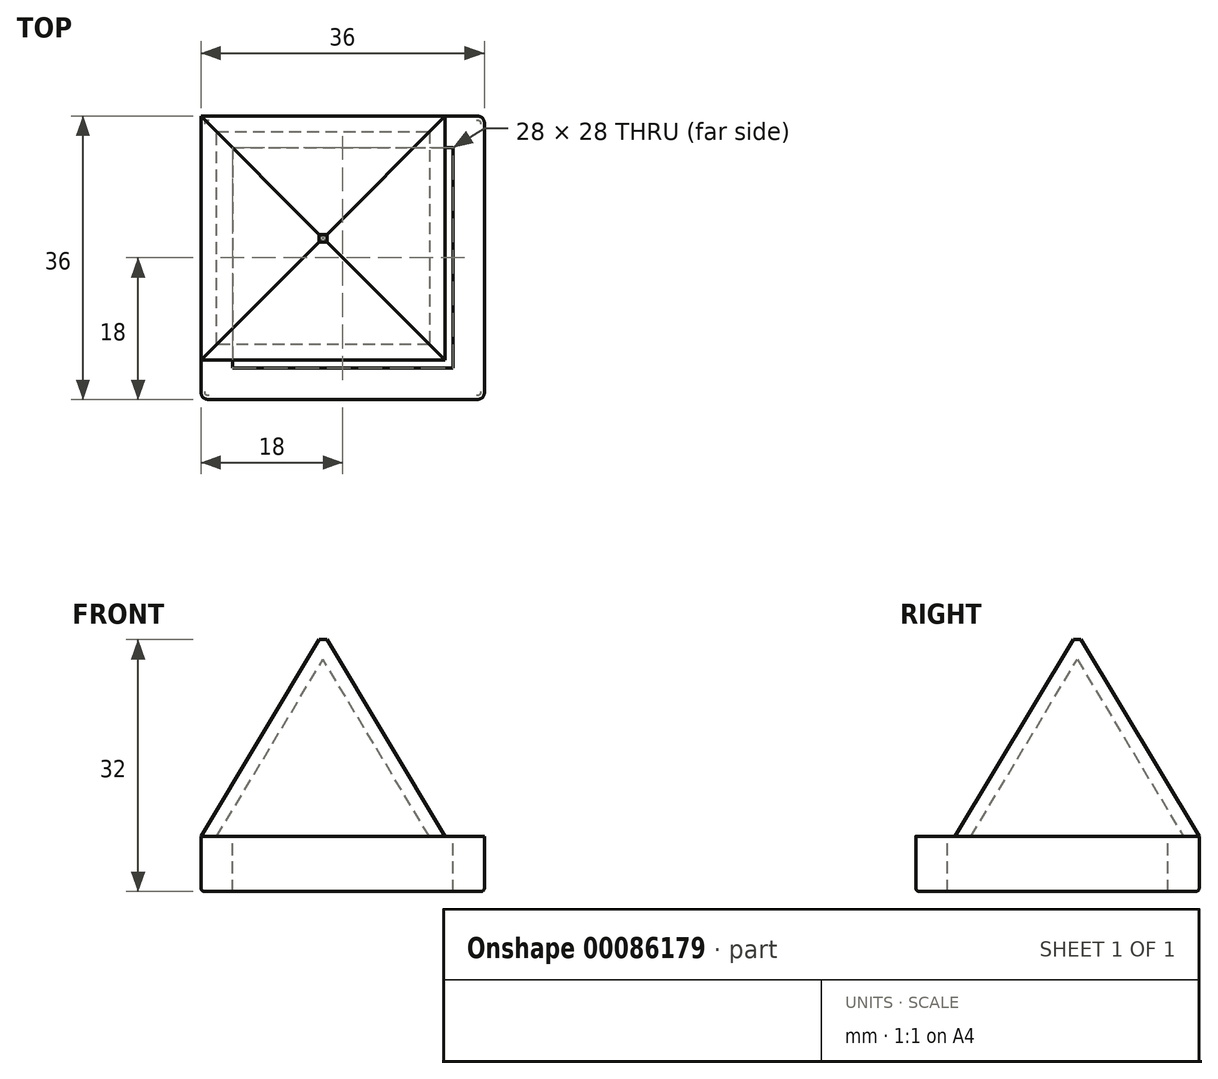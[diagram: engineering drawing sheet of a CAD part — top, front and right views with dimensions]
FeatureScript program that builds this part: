
annotation { "Feature Type Name" : "Feature", "Feature Type Description" : "" }
export const myFeature = defineFeature(function(context is Context, id is Id, definition is map)
    precondition{}
    {
        {
            var Q0;
            Q0=qCreatedBy(makeId("Top.planeOp"),FACE);
            var sketch = newSketch(context, id + "F0", { "sketchPlane" : qUnion([Q0])});
            skLineSegment(sketch, "E0.bottom", {"start": v(0, 0) * mm, "end": v(31, 0) * mm});
            skLineSegment(sketch, "E0.top", {"start": v(0, -31) * mm, "end": v(31, -31) * mm});
            skLineSegment(sketch, "E0.left", {"start": v(0, 0) * mm, "end": v(0, -31) * mm});
            skLineSegment(sketch, "E0.right", {"start": v(31, 0) * mm, "end": v(31, -31) * mm});
            skLineSegment(sketch, "E1.0", {"start": v(29, -2) * mm, "end": v(29, -29) * mm});
            skLineSegment(sketch, "E1.1", {"start": v(2, -2) * mm, "end": v(29, -2) * mm});
            skLineSegment(sketch, "E1.2", {"start": v(2, -2) * mm, "end": v(2, -29) * mm});
            skLineSegment(sketch, "E1.3", {"start": v(2, -29) * mm, "end": v(29, -29) * mm});
            skSolve(sketch);
        }
        {
            var Q0;
            Q0=makeQuery(id+"F0.imprint","IMPRINT",FACE,{"disambiguationData":[TD([[makeQuery(id+"F0.imprint","IMPRINT",EDGE,{"derivedFrom":sQuery(id+"F0.wireOp",EDGE,"E0.bottom")}),-1.0]])]});
            var Q1;
            Q1=makeQuery(id+"F0.imprint","IMPRINT",FACE,{"disambiguationData":[TD([[makeQuery(id+"F0.imprint","IMPRINT",EDGE,{"derivedFrom":sQuery(id+"F0.wireOp",EDGE,"E1.0")}),-1.0]])]});
            extrude(context, id + "F1", {"entities" : qUnion([Q0, Q1]), "depth" : 25 * mm, "hasDraft" : true, "draftAngle" : 31 * degree, "draftPullDirection" : true});
        }
        {
            var Q0;
            Q0=makeQuery(id+"F0.imprint","IMPRINT",FACE,{"disambiguationData":[TD([[makeQuery(id+"F0.imprint","IMPRINT",EDGE,{"derivedFrom":sQuery(id+"F0.wireOp",EDGE,"E1.0")}),-1.0]])]});
            extrude(context, id + "F2", {"entities" : qUnion([Q0]), "operationType" : NewBodyOperationType.REMOVE, "depth" : 25 * mm, "hasDraft" : true, "draftAngle" : 31 * degree, "draftPullDirection" : true});
        }
        {
            var Q0;
            Q0=qCreatedBy(makeId("Top.planeOp"),FACE);
            var sketch = newSketch(context, id + "F3", { "sketchPlane" : qUnion([Q0])});
            skLineSegment(sketch, "E2.bottom", {"start": v(0, 0) * mm, "end": v(36, 0) * mm});
            skLineSegment(sketch, "E2.top", {"start": v(0, -36) * mm, "end": v(36, -36) * mm});
            skLineSegment(sketch, "E2.left", {"start": v(0, 0) * mm, "end": v(0, -36) * mm});
            skLineSegment(sketch, "E2.right", {"start": v(36, 0) * mm, "end": v(36, -36) * mm});
            skLineSegment(sketch, "E3.0", {"start": v(32, -4) * mm, "end": v(32, -32) * mm});
            skLineSegment(sketch, "E3.1", {"start": v(4, -4) * mm, "end": v(32, -4) * mm});
            skLineSegment(sketch, "E3.2", {"start": v(4, -4) * mm, "end": v(4, -32) * mm});
            skLineSegment(sketch, "E3.3", {"start": v(4, -32) * mm, "end": v(32, -32) * mm});
            skSolve(sketch);
        }
        {
            var Q0;
            Q0=makeQuery(id+"F3.imprint","IMPRINT",FACE,{"disambiguationData":[TD([[makeQuery(id+"F3.imprint","IMPRINT",EDGE,{"derivedFrom":sQuery(id+"F3.wireOp",EDGE,"E2.bottom")}),-1.0]])]});
            extrude(context, id + "F4", {"entities" : qUnion([Q0]), "oppositeDirection" : true, "depth" : 7 * mm});
        }
        {
            var Q0;
            Q0=makeQuery(id+"F4.opExtrude","SWEPT_EDGE",EDGE,{"disambiguationData":[OSD([sQuery(id+"F3.wireOp",EDGE,"E2.top"),sQuery(id+"F3.wireOp",EDGE,"E2.right")])]});
            var Q1;
            Q1=makeQuery(id+"F4.opExtrude","SWEPT_EDGE",EDGE,{"disambiguationData":[OSD([sQuery(id+"F3.wireOp",EDGE,"E2.bottom"),sQuery(id+"F3.wireOp",EDGE,"E2.left")])]});
            var Q2;
            Q2=makeQuery(id+"F4.opExtrude","SWEPT_EDGE",EDGE,{"disambiguationData":[OSD([sQuery(id+"F3.wireOp",EDGE,"E2.bottom"),sQuery(id+"F3.wireOp",EDGE,"E2.right")])]});
            var Q3;
            Q3=makeQuery(id+"F4.opExtrude","SWEPT_EDGE",EDGE,{"disambiguationData":[OSD([sQuery(id+"F3.wireOp",EDGE,"E2.top"),sQuery(id+"F3.wireOp",EDGE,"E2.left")])]});
            fillet(context, id + "F5", {"entities" : qUnion([Q0, Q1, Q2, Q3]), "radius" : 1 * mm, "tangentPropagation" : true, "rho" : 0.5, "crossSection" : FilletCrossSection.CONIC, "allowEdgeOverflow" : false});
        }
        {
            var Q0;
            Q0=makeQuery(id+"F4.opExtrude","CAP_EDGE",EDGE,{"disambiguationData":[OSD([sQuery(id+"F3.wireOp",EDGE,"E2.left")])],"isStart":false});
            var Q1;
            Q1=makeQuery(id+"F4.opExtrude","CAP_EDGE",EDGE,{"disambiguationData":[OSD([sQuery(id+"F3.wireOp",EDGE,"E2.top")])],"isStart":false});
            var Q2;
            Q2=makeQuery(id+"F4.opExtrude","CAP_EDGE",EDGE,{"disambiguationData":[OSD([sQuery(id+"F3.wireOp",EDGE,"E2.right")])],"isStart":false});
            var Q3;
            Q3=makeQuery(id+"F4.opExtrude","CAP_EDGE",EDGE,{"disambiguationData":[OSD([sQuery(id+"F3.wireOp",EDGE,"E2.bottom")])],"isStart":false});
            fillet(context, id + "F6", {"entities" : qUnion([Q0, Q1, Q2, Q3]), "radius" : 0.5 * mm, "tangentPropagation" : true, "rho" : 0.5, "crossSection" : FilletCrossSection.CONIC, "allowEdgeOverflow" : false});
        }
    });
